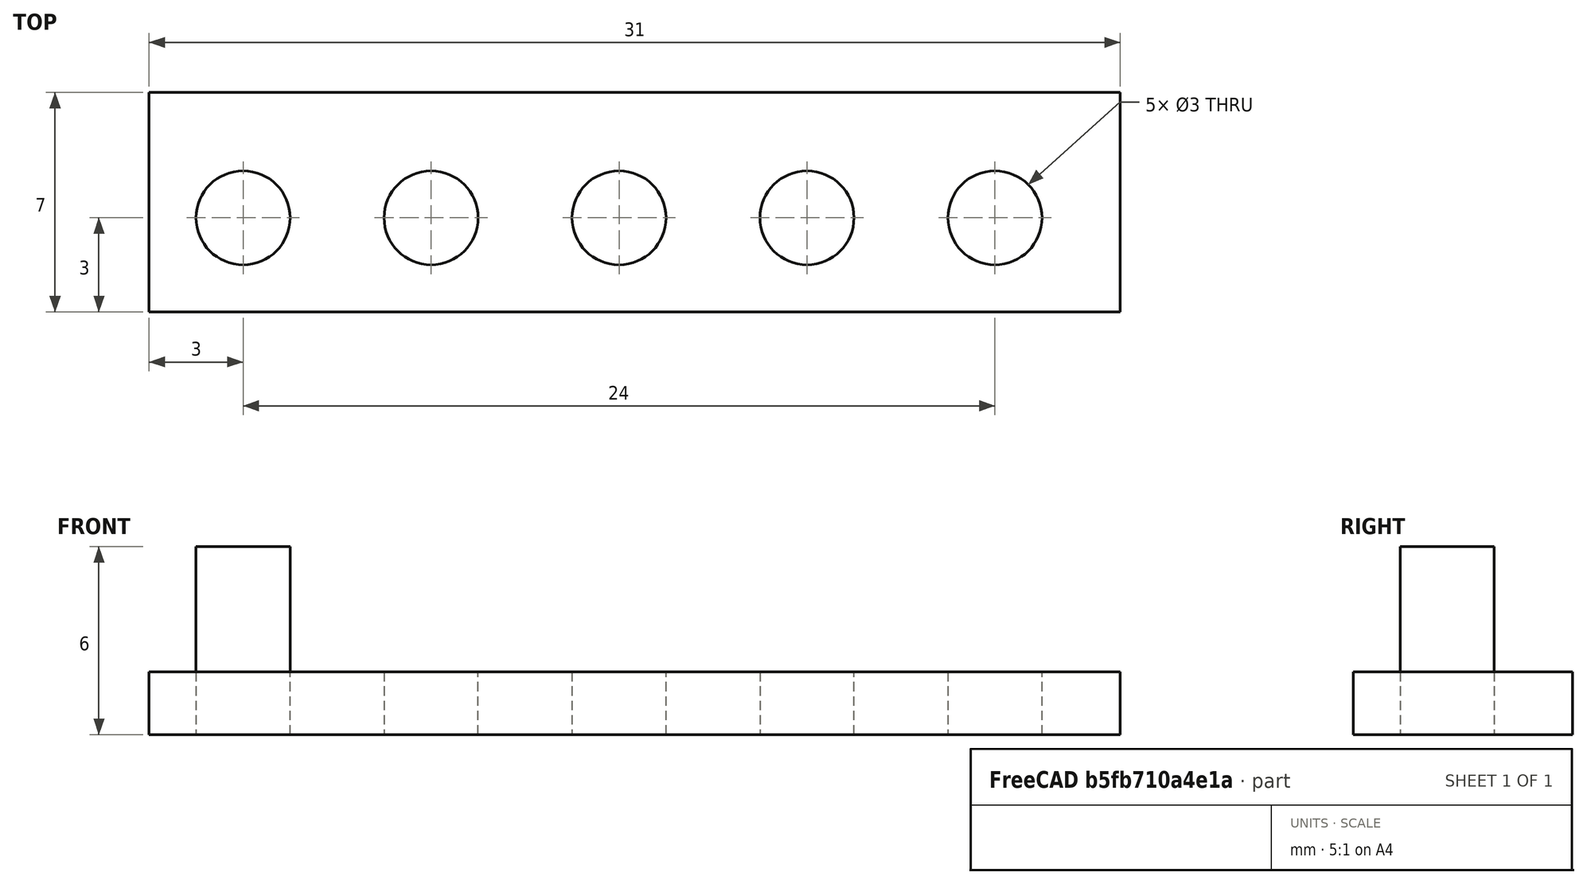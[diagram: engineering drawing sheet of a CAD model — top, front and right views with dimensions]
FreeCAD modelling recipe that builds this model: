
FCSTD DOCUMENT  (FreeCAD 0.21R33694 (Git))
Label: OJT1_T10R01_taladro
License: All rights reserved
LicenseURL: http://en.wikipedia.org/wiki/All_rights_reserved
objects: Part::Cylinder×1, Part::Box×1, Part::FeaturePython×1, Part::Cut×1
note: 3 computed .brp shape members not serialized (recipe doc carries the construction recipe); baked Part::Feature solids carry a one-line shape summary decoded from their .brp

FEATURE [Part::Cylinder] Cylinder
  Angle = 360
  AttacherType = Attacher::AttachEngine3D
  FirstAngle = 0
  Height = 6
  Radius = 1.5
  SecondAngle = 0
FEATURE [Part::Box] Box  label="Cube"
  AttacherType = Attacher::AttachEngine3D
  Height = 2
  Length = 31
  Placement = pos=(-3,-3,0) rot=(0,0,1;0rad)
  Width = 7
FEATURE [Part::FeaturePython] Array  # Draft array (typed FeaturePython)
  AlwaysSyncPlacement = false
  Angle = 360
  ArrayType = 0
  Axis = (0,0,1)
  Base = -> Cylinder
  Center = (0,0,0)
  Count = 5
  ExpandArray = false
  Fuse = false
  IntervalAxis = (0,0,0)
  IntervalX = (6,0,0)
  IntervalY = (0,100,0)
  IntervalZ = (0,0,100)
  NumberCircles = 3
  NumberPolar = 5
  NumberX = 5
  NumberY = 1
  NumberZ = 1
  PlacementList = 5 placements: arithmetic series from (0,0,0) step (6,0,0) to (24,0,0)
  RadialDistance = 50
  ScaleList = (5) [(1,1,1),(1,1,1),(1,1,1),(1,1,1),(1,1,1)]
  Symmetry = 1
  TangentialDistance = 25
FEATURE [Part::Cut] Cut
  Base = -> Box
  Refine = true
  Tool = -> Array
